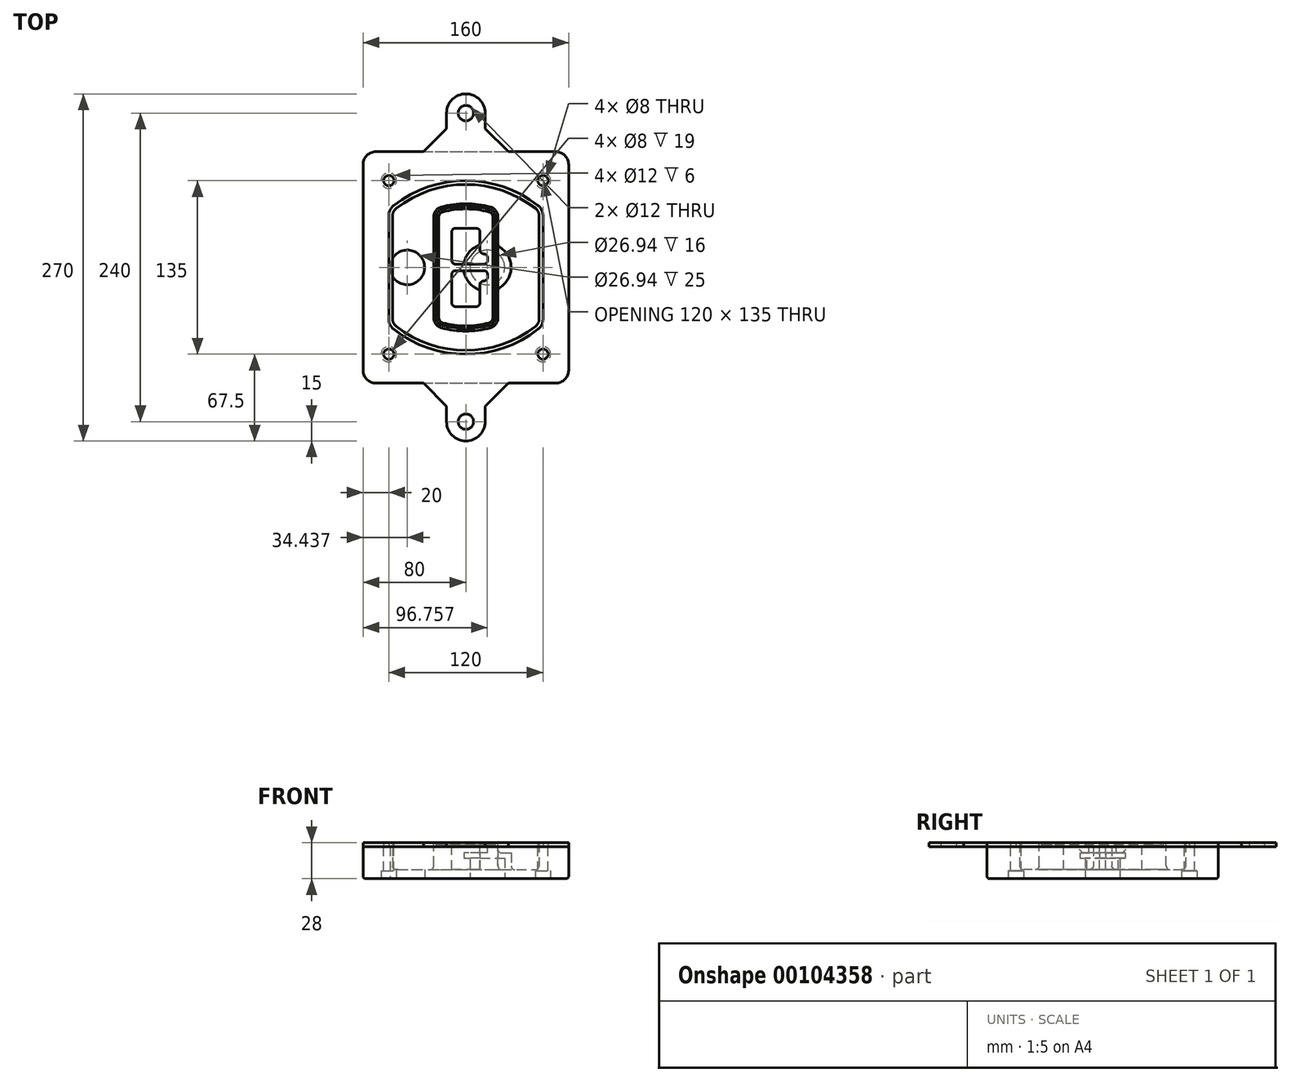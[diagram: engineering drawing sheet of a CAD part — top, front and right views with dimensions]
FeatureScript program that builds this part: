
annotation { "Feature Type Name" : "Feature", "Feature Type Description" : "" }
export const myFeature = defineFeature(function(context is Context, id is Id, definition is map)
    precondition{}
    {
        {
            var Q0;
            Q0=qCreatedBy(makeId("Top.planeOp"),FACE);
            var sketch = newSketch(context, id + "F0", { "sketchPlane" : qUnion([Q0])});
            skPoint(sketch, "E0.rect.middle", {"position": v(0, 0) * mm});
            skLineSegment(sketch, "E1.bottom", {"start": v(-70, -90) * mm, "end": v(70, -90) * mm});
            skLineSegment(sketch, "E1.top", {"start": v(-70, 90) * mm, "end": v(70, 90) * mm});
            skLineSegment(sketch, "E1.left", {"start": v(-80, -80) * mm, "end": v(-80, 80) * mm});
            skLineSegment(sketch, "E1.right", {"start": v(80, -80) * mm, "end": v(80, 80) * mm});
            skLineSegment(sketch, "E2", {"start": v(-80, 90) * mm, "end": v(80, -90) * mm, "construction": true});
            skLineSegment(sketch, "E3", {"start": v(80, 90) * mm, "end": v(-80, -90) * mm, "construction": true});
            skCircle(sketch, "E4", {"center": v(-60, 67.5) * mm, "radius": 4 * mm});
            skCircle(sketch, "E5", {"center": v(60, 67.5) * mm, "radius": 4 * mm});
            skCircle(sketch, "E6", {"center": v(60, -67.5) * mm, "radius": 4 * mm});
            skCircle(sketch, "E7", {"center": v(-60, -67.5) * mm, "radius": 4 * mm});
            skLineSegment(sketch, "E8", {"start": v(-60, 67.5) * mm, "end": v(60, 67.5) * mm, "construction": true});
            skLineSegment(sketch, "E9", {"start": v(60, 67.5) * mm, "end": v(60, -67.5) * mm, "construction": true});
            skLineSegment(sketch, "E10", {"start": v(60, -67.5) * mm, "end": v(-60, -67.5) * mm, "construction": true});
            skLineSegment(sketch, "E11", {"start": v(-60, -67.5) * mm, "end": v(-60, 67.5) * mm, "construction": true});
            skLineSegment(sketch, "E12", {"start": v(-60, 40.3) * mm, "end": v(-60, -40.3) * mm});
            skLineSegment(sketch, "E13", {"start": v(60, 40.3) * mm, "end": v(60, -40.3) * mm});
            skArc(sketch, "E14", {"start": v(56.15, 48.18) * mm, "mid": v(0, 67.5) * mm, "end": v(-56.15, 48.18) * mm});
            skArc(sketch, "E15", {"start": v(-56.15, -48.18) * mm, "mid": v(0, -67.5) * mm, "end": v(56.15, -48.18) * mm});
            skLineSegment(sketch, "E16", {"start": v(-60, 0) * mm, "end": v(60, 0) * mm, "construction": true});
            skPoint(sketch, "E17.visualSharp", {"position": v(-60, -45) * mm});
            skArc(sketch, "E17.filletArc", {"start": v(-60, -40.3) * mm, "mid": v(-58.99, -44.68) * mm, "end": v(-56.15, -48.18) * mm});
            skPoint(sketch, "E18.visualSharp", {"position": v(-60, 45) * mm});
            skArc(sketch, "E18.filletArc", {"start": v(-56.15, 48.18) * mm, "mid": v(-58.99, 44.68) * mm, "end": v(-60, 40.3) * mm});
            skPoint(sketch, "E19.visualSharp", {"position": v(60, 45) * mm});
            skArc(sketch, "E19.filletArc", {"start": v(60, 40.3) * mm, "mid": v(58.99, 44.68) * mm, "end": v(56.15, 48.18) * mm});
            skPoint(sketch, "E20.visualSharp", {"position": v(60, -45) * mm});
            skArc(sketch, "E20.filletArc", {"start": v(56.15, -48.18) * mm, "mid": v(58.99, -44.68) * mm, "end": v(60, -40.3) * mm});
            skPoint(sketch, "E21.visualSharp", {"position": v(-80, 90) * mm});
            skArc(sketch, "E21.filletArc", {"start": v(-70, 90) * mm, "mid": v(-77.07, 87.07) * mm, "end": v(-80, 80) * mm});
            skPoint(sketch, "E22.visualSharp", {"position": v(80, 90) * mm});
            skArc(sketch, "E22.filletArc", {"start": v(80, 80) * mm, "mid": v(77.07, 87.07) * mm, "end": v(70, 90) * mm});
            skPoint(sketch, "E23.visualSharp", {"position": v(80, -90) * mm});
            skArc(sketch, "E23.filletArc", {"start": v(70, -90) * mm, "mid": v(77.07, -87.07) * mm, "end": v(80, -80) * mm});
            skPoint(sketch, "E24.visualSharp", {"position": v(-80, -90) * mm});
            skArc(sketch, "E24.filletArc", {"start": v(-80, -80) * mm, "mid": v(-77.07, -87.07) * mm, "end": v(-70, -90) * mm});
            skArc(sketch, "E25.0", {"start": v(57, 40.3) * mm, "mid": v(56.3, 43.36) * mm, "end": v(54.3, 45.81) * mm});
            skLineSegment(sketch, "E25.1", {"start": v(57, 40.3) * mm, "end": v(57, -40.3) * mm});
            skArc(sketch, "E25.2", {"start": v(54.3, -45.81) * mm, "mid": v(56.3, -43.36) * mm, "end": v(57, -40.3) * mm});
            skArc(sketch, "E25.3", {"start": v(-54.3, -45.81) * mm, "mid": v(0, -64.5) * mm, "end": v(54.3, -45.81) * mm});
            skArc(sketch, "E25.4", {"start": v(-57, -40.3) * mm, "mid": v(-56.3, -43.36) * mm, "end": v(-54.3, -45.81) * mm});
            skArc(sketch, "E25.5", {"start": v(54.3, 45.81) * mm, "mid": v(0, 64.5) * mm, "end": v(-54.3, 45.81) * mm});
            skLineSegment(sketch, "E25.6", {"start": v(-57, 40.3) * mm, "end": v(-57, -40.3) * mm});
            skArc(sketch, "E25.7", {"start": v(-54.3, 45.81) * mm, "mid": v(-56.3, 43.36) * mm, "end": v(-57, 40.3) * mm});
            skArc(sketch, "E26.0", {"start": v(-58.62, 51.33) * mm, "mid": v(-62.58, 46.43) * mm, "end": v(-64, 40.3) * mm});
            skArc(sketch, "E26.1", {"start": v(58.62, 51.33) * mm, "mid": v(0, 71.5) * mm, "end": v(-58.62, 51.33) * mm});
            skArc(sketch, "E26.2", {"start": v(64, 40.3) * mm, "mid": v(62.58, 46.43) * mm, "end": v(58.62, 51.33) * mm});
            skLineSegment(sketch, "E26.3", {"start": v(64, 40.3) * mm, "end": v(64, -40.3) * mm});
            skArc(sketch, "E26.4", {"start": v(58.62, -51.33) * mm, "mid": v(62.58, -46.43) * mm, "end": v(64, -40.3) * mm});
            skLineSegment(sketch, "E26.5", {"start": v(-64, 40.3) * mm, "end": v(-64, -40.3) * mm});
            skArc(sketch, "E26.6", {"start": v(-58.62, -51.33) * mm, "mid": v(0, -71.5) * mm, "end": v(58.62, -51.33) * mm});
            skArc(sketch, "E26.7", {"start": v(-64, -40.3) * mm, "mid": v(-62.58, -46.43) * mm, "end": v(-58.62, -51.33) * mm});
            skSolve(sketch);
        }
        {
            var Q0;
            Q0=makeQuery(id+"F0.imprint","IMPRINT",FACE,{"disambiguationData":[TD([[makeQuery(id+"F0.imprint","IMPRINT",EDGE,{"derivedFrom":sQuery(id+"F0.wireOp",EDGE,"E1.bottom")}),1.0]])]});
            var Q1;
            Q1=makeQuery(id+"F0.imprint","IMPRINT",FACE,{"disambiguationData":[TD([[makeQuery(id+"F0.imprint","IMPRINT",EDGE,{"derivedFrom":sQuery(id+"F0.wireOp",EDGE,"E12")}),1.0]])]});
            var Q2;
            Q2=makeQuery(id+"F0.imprint","IMPRINT",FACE,{"disambiguationData":[TD([[makeQuery(id+"F0.imprint","IMPRINT",EDGE,{"derivedFrom":sQuery(id+"F0.wireOp",EDGE,"E25.0")}),1.0]])]});
            var Q3;
            Q3=makeQuery(id+"F0.imprint","IMPRINT",FACE,{"disambiguationData":[TD([[makeQuery(id+"F0.imprint","IMPRINT",EDGE,{"derivedFrom":sQuery(id+"F0.wireOp",EDGE,"E12")}),-1.0]])]});
            extrude(context, id + "F1", {"entities" : qUnion([Q0, Q1, Q2, Q3]), "oppositeDirection" : true, "depth" : 25 * mm});
        }
        {
            var Q0;
            Q0=makeQuery(id+"F0.imprint","IMPRINT",FACE,{"disambiguationData":[TD([[makeQuery(id+"F0.imprint","IMPRINT",EDGE,{"derivedFrom":sQuery(id+"F0.wireOp",EDGE,"E12")}),1.0]])]});
            extrude(context, id + "F2", {"entities" : qUnion([Q0]), "operationType" : NewBodyOperationType.ADD, "depth" : 3 * mm});
        }
        {
            var Q0;
            Q0=makeQuery(id+"F0.imprint","IMPRINT",FACE,{"disambiguationData":[TD([[makeQuery(id+"F0.imprint","IMPRINT",EDGE,{"derivedFrom":sQuery(id+"F0.wireOp",EDGE,"E25.0")}),1.0]])]});
            extrude(context, id + "F3", {"entities" : qUnion([Q0]), "operationType" : NewBodyOperationType.REMOVE, "oppositeDirection" : true, "depth" : 18 * mm});
        }
        {
            var Q0;
            Q0=makeQuery(id+"F2.opExtrude","CAP_FACE",FACE,{"disambiguationData":[OSD([sQuery(id+"F0.wireOp",EDGE,"E12"),sQuery(id+"F0.wireOp",EDGE,"E13"),sQuery(id+"F0.wireOp",EDGE,"E14"),sQuery(id+"F0.wireOp",EDGE,"E15"),sQuery(id+"F0.wireOp",EDGE,"E17.filletArc"),sQuery(id+"F0.wireOp",EDGE,"E18.filletArc"),sQuery(id+"F0.wireOp",EDGE,"E19.filletArc"),sQuery(id+"F0.wireOp",EDGE,"E20.filletArc"),sQuery(id+"F0.wireOp",EDGE,"E25.0"),sQuery(id+"F0.wireOp",EDGE,"E25.1"),sQuery(id+"F0.wireOp",EDGE,"E25.2"),sQuery(id+"F0.wireOp",EDGE,"E25.3"),sQuery(id+"F0.wireOp",EDGE,"E25.4"),sQuery(id+"F0.wireOp",EDGE,"E25.5"),sQuery(id+"F0.wireOp",EDGE,"E25.6"),sQuery(id+"F0.wireOp",EDGE,"E25.7")])],"isStart":false});
            var sketch = newSketch(context, id + "F4", { "sketchPlane" : qUnion([Q0])});
            skArc(sketch, "E27.0", {"start": v(-19.08, -46.97) * mm, "mid": v(0, -49.5) * mm, "end": v(19.08, -46.97) * mm});
            skArc(sketch, "E28.0", {"start": v(19.08, 46.97) * mm, "mid": v(0, 49.5) * mm, "end": v(-19.08, 46.97) * mm});
            skLineSegment(sketch, "E29", {"start": v(-25, 39.25) * mm, "end": v(-25, -39.25) * mm});
            skLineSegment(sketch, "E30", {"start": v(25, 39.25) * mm, "end": v(25, -39.25) * mm});
            skLineSegment(sketch, "E31", {"start": v(-25, 45.1) * mm, "end": v(25, 45.1) * mm, "construction": true});
            skLineSegment(sketch, "E32", {"start": v(-25, -45.1) * mm, "end": v(25, -45.1) * mm, "construction": true});
            skPoint(sketch, "E33.visualSharp", {"position": v(-25, 45.1) * mm});
            skArc(sketch, "E33.filletArc", {"start": v(-19.08, 46.97) * mm, "mid": v(-23.35, 44.11) * mm, "end": v(-25, 39.25) * mm});
            skPoint(sketch, "E34.visualSharp", {"position": v(25, 45.1) * mm});
            skArc(sketch, "E34.filletArc", {"start": v(25, 39.25) * mm, "mid": v(23.35, 44.11) * mm, "end": v(19.08, 46.97) * mm});
            skPoint(sketch, "E35.visualSharp", {"position": v(25, -45.1) * mm});
            skArc(sketch, "E35.filletArc", {"start": v(19.08, -46.97) * mm, "mid": v(23.35, -44.11) * mm, "end": v(25, -39.25) * mm});
            skPoint(sketch, "E36.visualSharp", {"position": v(-25, -45.1) * mm});
            skArc(sketch, "E36.filletArc", {"start": v(-25, -39.25) * mm, "mid": v(-23.35, -44.11) * mm, "end": v(-19.08, -46.97) * mm});
            skArc(sketch, "E37.0", {"start": v(54.3, 45.81) * mm, "mid": v(0, 64.5) * mm, "end": v(-54.3, 45.81) * mm});
            skArc(sketch, "E37.1", {"start": v(-54.3, 45.81) * mm, "mid": v(-56.3, 43.36) * mm, "end": v(-57, 40.3) * mm});
            skLineSegment(sketch, "E37.2", {"start": v(-57, 40.3) * mm, "end": v(-57, -40.3) * mm});
            skArc(sketch, "E37.3", {"start": v(-57, -40.3) * mm, "mid": v(-56.3, -43.36) * mm, "end": v(-54.3, -45.81) * mm});
            skArc(sketch, "E37.4", {"start": v(-54.3, -45.81) * mm, "mid": v(0, -64.5) * mm, "end": v(54.3, -45.81) * mm});
            skArc(sketch, "E37.5", {"start": v(54.3, -45.81) * mm, "mid": v(56.3, -43.36) * mm, "end": v(57, -40.3) * mm});
            skLineSegment(sketch, "E37.6", {"start": v(57, 40.3) * mm, "end": v(57, -40.3) * mm});
            skArc(sketch, "E37.7", {"start": v(57, 40.3) * mm, "mid": v(56.3, 43.36) * mm, "end": v(54.3, 45.81) * mm});
            skLineSegment(sketch, "E38.0", {"start": v(23, 39.25) * mm, "end": v(23, -39.25) * mm});
            skArc(sketch, "E38.1", {"start": v(18.56, -45.04) * mm, "mid": v(21.76, -42.9) * mm, "end": v(23, -39.25) * mm});
            skArc(sketch, "E38.2", {"start": v(-18.56, -45.04) * mm, "mid": v(0, -47.5) * mm, "end": v(18.56, -45.04) * mm});
            skArc(sketch, "E38.3", {"start": v(-23, -39.25) * mm, "mid": v(-21.76, -42.9) * mm, "end": v(-18.56, -45.04) * mm});
            skLineSegment(sketch, "E38.4", {"start": v(-23, 39.25) * mm, "end": v(-23, -39.25) * mm});
            skArc(sketch, "E38.5", {"start": v(23, 39.25) * mm, "mid": v(21.76, 42.9) * mm, "end": v(18.56, 45.04) * mm});
            skArc(sketch, "E38.6", {"start": v(-18.56, 45.04) * mm, "mid": v(-21.76, 42.9) * mm, "end": v(-23, 39.25) * mm});
            skArc(sketch, "E38.7", {"start": v(18.56, 45.04) * mm, "mid": v(0, 47.5) * mm, "end": v(-18.56, 45.04) * mm});
            skArc(sketch, "E39.0", {"start": v(21, 39.25) * mm, "mid": v(20.18, 41.68) * mm, "end": v(18.04, 43.1) * mm});
            skLineSegment(sketch, "E39.1", {"start": v(21, 39.25) * mm, "end": v(21, -39.25) * mm});
            skArc(sketch, "E39.2", {"start": v(18.04, -43.1) * mm, "mid": v(20.18, -41.68) * mm, "end": v(21, -39.25) * mm});
            skArc(sketch, "E39.3", {"start": v(-18.04, -43.1) * mm, "mid": v(0, -45.5) * mm, "end": v(18.04, -43.1) * mm});
            skArc(sketch, "E39.4", {"start": v(-21, -39.25) * mm, "mid": v(-20.18, -41.68) * mm, "end": v(-18.04, -43.1) * mm});
            skArc(sketch, "E39.5", {"start": v(18.04, 43.1) * mm, "mid": v(0, 45.5) * mm, "end": v(-18.04, 43.1) * mm});
            skLineSegment(sketch, "E39.6", {"start": v(-21, 39.25) * mm, "end": v(-21, -39.25) * mm});
            skArc(sketch, "E39.7", {"start": v(-18.04, 43.1) * mm, "mid": v(-20.18, 41.68) * mm, "end": v(-21, 39.25) * mm});
            skLineSegment(sketch, "E40", {"start": v(-25, 0) * mm, "end": v(25, 0) * mm, "construction": true});
            skLineSegment(sketch, "E41", {"start": v(-11, 5.5) * mm, "end": v(-11, 27.5) * mm});
            skLineSegment(sketch, "E42", {"start": v(-8, 30.5) * mm, "end": v(8, 30.5) * mm});
            skLineSegment(sketch, "E43", {"start": v(11, 27.5) * mm, "end": v(11, 13.5) * mm});
            skLineSegment(sketch, "E44", {"start": v(14, 10.5) * mm, "end": v(14, 10.5) * mm});
            skLineSegment(sketch, "E45", {"start": v(17, 7.5) * mm, "end": v(17, 5.5) * mm});
            skLineSegment(sketch, "E46", {"start": v(14, 2.5) * mm, "end": v(-8, 2.5) * mm});
            skPoint(sketch, "E47.visualSharp", {"position": v(-11, 30.5) * mm});
            skArc(sketch, "E47.filletArc", {"start": v(-8, 30.5) * mm, "mid": v(-10.12, 29.62) * mm, "end": v(-11, 27.5) * mm});
            skPoint(sketch, "E48.visualSharp", {"position": v(11, 30.5) * mm});
            skArc(sketch, "E48.filletArc", {"start": v(11, 27.5) * mm, "mid": v(10.12, 29.62) * mm, "end": v(8, 30.5) * mm});
            skPoint(sketch, "E49.visualSharp", {"position": v(11, 10.5) * mm});
            skArc(sketch, "E49.filletArc", {"start": v(11, 13.5) * mm, "mid": v(11.88, 11.38) * mm, "end": v(14, 10.5) * mm});
            skPoint(sketch, "E50.visualSharp", {"position": v(17, 10.5) * mm});
            skArc(sketch, "E50.filletArc", {"start": v(17, 7.5) * mm, "mid": v(16.12, 9.62) * mm, "end": v(14, 10.5) * mm});
            skPoint(sketch, "E51.visualSharp", {"position": v(17, 2.5) * mm});
            skArc(sketch, "E51.filletArc", {"start": v(14, 2.5) * mm, "mid": v(16.12, 3.38) * mm, "end": v(17, 5.5) * mm});
            skPoint(sketch, "E52.visualSharp", {"position": v(-11, 2.5) * mm});
            skArc(sketch, "E52.filletArc", {"start": v(-11, 5.5) * mm, "mid": v(-10.12, 3.38) * mm, "end": v(-8, 2.5) * mm});
            skLineSegment(sketch, "E53.0.MirrorCS", {"start": v(14, -2.5) * mm, "end": v(-8, -2.5) * mm});
            skArc(sketch, "E54.0.MirrorCS", {"start": v(-11, -5.5) * mm, "mid": v(-10.12, -3.38) * mm, "end": v(-8, -2.5) * mm});
            skLineSegment(sketch, "E55.0.MirrorCS", {"start": v(-11, -5.5) * mm, "end": v(-11, -27.5) * mm});
            skArc(sketch, "E56.0.MirrorCS", {"start": v(-8, -30.5) * mm, "mid": v(-10.12, -29.62) * mm, "end": v(-11, -27.5) * mm});
            skLineSegment(sketch, "E57.0.MirrorCS", {"start": v(-8, -30.5) * mm, "end": v(8, -30.5) * mm});
            skArc(sketch, "E58.0.MirrorCS", {"start": v(11, -27.5) * mm, "mid": v(10.12, -29.62) * mm, "end": v(8, -30.5) * mm});
            skLineSegment(sketch, "E59.0.MirrorCS", {"start": v(11, -27.5) * mm, "end": v(11, -13.5) * mm});
            skArc(sketch, "E60.0.MirrorCS", {"start": v(11, -13.5) * mm, "mid": v(11.88, -11.38) * mm, "end": v(14, -10.5) * mm});
            skArc(sketch, "E61.0.MirrorCS", {"start": v(17, -7.5) * mm, "mid": v(16.12, -9.62) * mm, "end": v(14, -10.5) * mm});
            skLineSegment(sketch, "E62.0.MirrorCS", {"start": v(17, -7.5) * mm, "end": v(17, -5.5) * mm});
            skArc(sketch, "E63.0.MirrorCS", {"start": v(14, -2.5) * mm, "mid": v(16.12, -3.38) * mm, "end": v(17, -5.5) * mm});
            skSolve(sketch);
        }
        {
            var Q0;
            Q0=makeQuery(id+"F4.imprint","IMPRINT",FACE,{"disambiguationData":[TD([[makeQuery(id+"F4.imprint","IMPRINT",EDGE,{"derivedFrom":sQuery(id+"F4.wireOp",EDGE,"E27.0")}),1.0]])]});
            var Q1;
            Q1=makeQuery(id+"F4.imprint","IMPRINT",FACE,{"disambiguationData":[TD([[makeQuery(id+"F4.imprint","IMPRINT",EDGE,{"derivedFrom":sQuery(id+"F4.wireOp",EDGE,"E38.0")}),-1.0]])]});
            var Q2;
            Q2=makeQuery(id+"F4.imprint","IMPRINT",FACE,{"disambiguationData":[TD([[makeQuery(id+"F4.imprint","IMPRINT",EDGE,{"derivedFrom":sQuery(id+"F4.wireOp",EDGE,"E39.0")}),1.0]])]});
            extrude(context, id + "F5", {"entities" : qUnion([Q0, Q1, Q2]), "operationType" : NewBodyOperationType.ADD, "endBound" : BoundingType.UP_TO_NEXT, "oppositeDirection" : true, "depth" : 25 * mm});
        }
        {
            var Q0;
            Q0=makeQuery(id+"F4.imprint","IMPRINT",FACE,{"disambiguationData":[TD([[makeQuery(id+"F4.imprint","IMPRINT",EDGE,{"derivedFrom":sQuery(id+"F4.wireOp",EDGE,"E38.0")}),-1.0]])]});
            extrude(context, id + "F6", {"entities" : qUnion([Q0]), "operationType" : NewBodyOperationType.REMOVE, "oppositeDirection" : true, "depth" : 2 * mm});
        }
        {
            var Q0;
            Q0=makeQuery(id+"F1.opExtrude","CAP_FACE",FACE,{"disambiguationData":[OSD([sQuery(id+"F0.wireOp",EDGE,"E1.bottom"),sQuery(id+"F0.wireOp",EDGE,"E1.top"),sQuery(id+"F0.wireOp",EDGE,"E1.left"),sQuery(id+"F0.wireOp",EDGE,"E1.right"),sQuery(id+"F0.wireOp",EDGE,"E4"),sQuery(id+"F0.wireOp",EDGE,"E5"),sQuery(id+"F0.wireOp",EDGE,"E6"),sQuery(id+"F0.wireOp",EDGE,"E7"),sQuery(id+"F0.wireOp",EDGE,"E21.filletArc"),sQuery(id+"F0.wireOp",EDGE,"E22.filletArc"),sQuery(id+"F0.wireOp",EDGE,"E23.filletArc"),sQuery(id+"F0.wireOp",EDGE,"E24.filletArc")])],"isStart":false});
            var sketch = newSketch(context, id + "F7", { "sketchPlane" : qUnion([Q0])});
            skCircle(sketch, "E64", {"center": v(16.76, 0) * mm, "radius": 13.47 * mm});
            skCircle(sketch, "E65", {"center": v(-45.56, 0) * mm, "radius": 13.47 * mm});
            skLineSegment(sketch, "E66", {"start": v(80, 0) * mm, "end": v(-80, 0) * mm});
            skCircle(sketch, "E67", {"center": v(16.76, 0) * mm, "radius": 18.47 * mm});
            skCircle(sketch, "E68", {"center": v(60, -67.5) * mm, "radius": 6 * mm});
            skCircle(sketch, "E69", {"center": v(-60, -67.5) * mm, "radius": 6 * mm});
            skCircle(sketch, "E70", {"center": v(-60, 67.5) * mm, "radius": 6 * mm});
            skCircle(sketch, "E71", {"center": v(60, 67.5) * mm, "radius": 6 * mm});
            skSolve(sketch);
        }
        {
            var Q0;
            {var subQ1=sQuery(id+"F7.wireOp",EDGE,"E66");var subQ4=sQuery(id+"F7.wireOp",EDGE,"E64");var subQ6=makeQuery(id+"F7.imprint","INTERSECT",VERTEX,{"disambiguationData":[OD(0.0)],"derivedFrom":[subQ4,subQ1]});Q0=makeQuery(id+"F7.imprint","IMPRINT",FACE,{"disambiguationData":[TD([[makeQuery(id+"F7.imprint","IMPRINT",EDGE,{"disambiguationData":[TD([[subQ6,-1.0]])],"derivedFrom":subQ4}),-1.0]])]});}
            var Q1;
            {var subQ0=sQuery(id+"F7.wireOp",EDGE,"E66");var subQ1=sQuery(id+"F7.wireOp",EDGE,"E64");var subQ3=makeQuery(id+"F7.imprint","INTERSECT",VERTEX,{"disambiguationData":[OD(0.0)],"derivedFrom":[subQ1,subQ0]});Q1=makeQuery(id+"F7.imprint","IMPRINT",FACE,{"disambiguationData":[TD([[makeQuery(id+"F7.imprint","IMPRINT",EDGE,{"disambiguationData":[TD([[subQ3,-1.0]])],"derivedFrom":subQ1}),1.0]])]});}
            var Q2;
            {var subQ0=sQuery(id+"F7.wireOp",EDGE,"E66");var subQ1=sQuery(id+"F7.wireOp",EDGE,"E64");var subQ3=makeQuery(id+"F7.imprint","INTERSECT",VERTEX,{"disambiguationData":[OD(0.0)],"derivedFrom":[subQ1,subQ0]});Q2=makeQuery(id+"F7.imprint","IMPRINT",FACE,{"disambiguationData":[TD([[makeQuery(id+"F7.imprint","IMPRINT",EDGE,{"disambiguationData":[TD([[subQ3,1.0]])],"derivedFrom":subQ1}),1.0]])]});}
            var Q3;
            {var subQ1=sQuery(id+"F7.wireOp",EDGE,"E66");var subQ4=sQuery(id+"F7.wireOp",EDGE,"E64");var subQ6=makeQuery(id+"F7.imprint","INTERSECT",VERTEX,{"disambiguationData":[OD(0.0)],"derivedFrom":[subQ4,subQ1]});Q3=makeQuery(id+"F7.imprint","IMPRINT",FACE,{"disambiguationData":[TD([[makeQuery(id+"F7.imprint","IMPRINT",EDGE,{"disambiguationData":[TD([[subQ6,1.0]])],"derivedFrom":subQ4}),-1.0]])]});}
            extrude(context, id + "F8", {"entities" : qUnion([Q0, Q1, Q2, Q3]), "operationType" : NewBodyOperationType.ADD, "oppositeDirection" : true, "depth" : 20 * mm});
        }
        {
            var Q0;
            {var subQ0=sQuery(id+"F7.wireOp",EDGE,"E66");var subQ1=sQuery(id+"F7.wireOp",EDGE,"E64");var subQ3=makeQuery(id+"F7.imprint","INTERSECT",VERTEX,{"disambiguationData":[OD(0.0)],"derivedFrom":[subQ1,subQ0]});Q0=makeQuery(id+"F7.imprint","IMPRINT",FACE,{"disambiguationData":[TD([[makeQuery(id+"F7.imprint","IMPRINT",EDGE,{"disambiguationData":[TD([[subQ3,-1.0]])],"derivedFrom":subQ1}),1.0]])]});}
            var Q1;
            {var subQ0=sQuery(id+"F7.wireOp",EDGE,"E66");var subQ1=sQuery(id+"F7.wireOp",EDGE,"E64");var subQ3=makeQuery(id+"F7.imprint","INTERSECT",VERTEX,{"disambiguationData":[OD(0.0)],"derivedFrom":[subQ1,subQ0]});Q1=makeQuery(id+"F7.imprint","IMPRINT",FACE,{"disambiguationData":[TD([[makeQuery(id+"F7.imprint","IMPRINT",EDGE,{"disambiguationData":[TD([[subQ3,1.0]])],"derivedFrom":subQ1}),1.0]])]});}
            extrude(context, id + "F9", {"entities" : qUnion([Q0, Q1]), "operationType" : NewBodyOperationType.REMOVE, "oppositeDirection" : true, "depth" : 16 * mm});
        }
        {
            var Q0;
            {var subQ0=sQuery(id+"F7.wireOp",EDGE,"E66");var subQ1=sQuery(id+"F7.wireOp",EDGE,"E65");var subQ3=makeQuery(id+"F7.imprint","INTERSECT",VERTEX,{"disambiguationData":[OD(0.0)],"derivedFrom":[subQ1,subQ0]});Q0=makeQuery(id+"F7.imprint","IMPRINT",FACE,{"disambiguationData":[TD([[makeQuery(id+"F7.imprint","IMPRINT",EDGE,{"disambiguationData":[TD([[subQ3,-1.0]])],"derivedFrom":subQ1}),1.0]])]});}
            var Q1;
            {var subQ0=sQuery(id+"F7.wireOp",EDGE,"E66");var subQ1=sQuery(id+"F7.wireOp",EDGE,"E65");var subQ3=makeQuery(id+"F7.imprint","INTERSECT",VERTEX,{"disambiguationData":[OD(0.0)],"derivedFrom":[subQ1,subQ0]});Q1=makeQuery(id+"F7.imprint","IMPRINT",FACE,{"disambiguationData":[TD([[makeQuery(id+"F7.imprint","IMPRINT",EDGE,{"disambiguationData":[TD([[subQ3,1.0]])],"derivedFrom":subQ1}),1.0]])]});}
            extrude(context, id + "F10", {"entities" : qUnion([Q0, Q1]), "operationType" : NewBodyOperationType.REMOVE, "oppositeDirection" : true, "depth" : 25 * mm});
        }
        {
            var Q0;
            Q0=makeQuery(id+"F7.imprint","IMPRINT",FACE,{"disambiguationData":[TD([[makeQuery(id+"F7.imprint","IMPRINT",EDGE,{"derivedFrom":sQuery(id+"F7.wireOp",EDGE,"E68")}),1.0]])]});
            var Q1;
            Q1=makeQuery(id+"F7.imprint","IMPRINT",FACE,{"disambiguationData":[TD([[makeQuery(id+"F7.imprint","IMPRINT",EDGE,{"derivedFrom":makeQuery(id+"F1.opExtrude","CAP_EDGE",EDGE,{"disambiguationData":[OSD([sQuery(id+"F0.wireOp",EDGE,"E5")])],"isStart":false})}),-1.0]])]});
            var Q2;
            Q2=makeQuery(id+"F7.imprint","IMPRINT",FACE,{"disambiguationData":[TD([[makeQuery(id+"F7.imprint","IMPRINT",EDGE,{"derivedFrom":sQuery(id+"F7.wireOp",EDGE,"E69")}),1.0]])]});
            var Q3;
            Q3=makeQuery(id+"F7.imprint","IMPRINT",FACE,{"disambiguationData":[TD([[makeQuery(id+"F7.imprint","IMPRINT",EDGE,{"derivedFrom":makeQuery(id+"F1.opExtrude","CAP_EDGE",EDGE,{"disambiguationData":[OSD([sQuery(id+"F0.wireOp",EDGE,"E4")])],"isStart":false})}),-1.0]])]});
            var Q4;
            Q4=makeQuery(id+"F7.imprint","IMPRINT",FACE,{"disambiguationData":[TD([[makeQuery(id+"F7.imprint","IMPRINT",EDGE,{"derivedFrom":sQuery(id+"F7.wireOp",EDGE,"E70")}),1.0]])]});
            var Q5;
            Q5=makeQuery(id+"F7.imprint","IMPRINT",FACE,{"disambiguationData":[TD([[makeQuery(id+"F7.imprint","IMPRINT",EDGE,{"derivedFrom":makeQuery(id+"F1.opExtrude","CAP_EDGE",EDGE,{"disambiguationData":[OSD([sQuery(id+"F0.wireOp",EDGE,"E7")])],"isStart":false})}),-1.0]])]});
            var Q6;
            Q6=makeQuery(id+"F7.imprint","IMPRINT",FACE,{"disambiguationData":[TD([[makeQuery(id+"F7.imprint","IMPRINT",EDGE,{"derivedFrom":sQuery(id+"F7.wireOp",EDGE,"E71")}),1.0]])]});
            var Q7;
            Q7=makeQuery(id+"F7.imprint","IMPRINT",FACE,{"disambiguationData":[TD([[makeQuery(id+"F7.imprint","IMPRINT",EDGE,{"derivedFrom":makeQuery(id+"F1.opExtrude","CAP_EDGE",EDGE,{"disambiguationData":[OSD([sQuery(id+"F0.wireOp",EDGE,"E6")])],"isStart":false})}),-1.0]])]});
            extrude(context, id + "F11", {"entities" : qUnion([Q0, Q1, Q2, Q3, Q4, Q5, Q6, Q7]), "operationType" : NewBodyOperationType.REMOVE, "oppositeDirection" : true, "depth" : 6 * mm});
        }
        {
            var Q0;
            Q0=makeQuery(id+"F9.boolean.opBoolean","COPY",FACE,{"derivedFrom":makeQuery(id+"F9.opExtrude","CAP_FACE",FACE,{"disambiguationData":[OSD([sQuery(id+"F7.wireOp",EDGE,"E64")])],"isStart":false})});
            var sketch = newSketch(context, id + "F12", { "sketchPlane" : qUnion([Q0])});
            skArc(sketch, "E72.0", {"start": v(11, 17.55) * mm, "mid": v(2.57, 11.82) * mm, "end": v(-1.54, 2.5) * mm});
            skArc(sketch, "E72.1", {"start": v(-1.54, -2.5) * mm, "mid": v(2.57, -11.82) * mm, "end": v(11, -17.55) * mm});
            skLineSegment(sketch, "E73", {"start": v(-1.54, -2.5) * mm, "end": v(14, -2.5) * mm});
            skLineSegment(sketch, "E74.0", {"start": v(14, 2.5) * mm, "end": v(-1.54, 2.5) * mm});
            skArc(sketch, "E74.1", {"start": v(14, 2.5) * mm, "mid": v(16.12, 3.38) * mm, "end": v(17, 5.5) * mm});
            skLineSegment(sketch, "E74.2", {"start": v(17, 7.5) * mm, "end": v(17, 5.5) * mm});
            skArc(sketch, "E74.3", {"start": v(17, 7.5) * mm, "mid": v(16.12, 9.62) * mm, "end": v(14, 10.5) * mm});
            skArc(sketch, "E74.4", {"start": v(11, 13.5) * mm, "mid": v(11.88, 11.38) * mm, "end": v(14, 10.5) * mm});
            skLineSegment(sketch, "E74.5", {"start": v(11, 17.55) * mm, "end": v(11, 13.5) * mm});
            skLineSegment(sketch, "E74.7", {"start": v(14, -2.5) * mm, "end": v(-1.54, -2.5) * mm});
            skArc(sketch, "E74.8", {"start": v(14, -2.5) * mm, "mid": v(16.12, -3.38) * mm, "end": v(17, -5.5) * mm});
            skLineSegment(sketch, "E74.9", {"start": v(17, -7.5) * mm, "end": v(17, -5.5) * mm});
            skArc(sketch, "E74.10", {"start": v(17, -7.5) * mm, "mid": v(16.12, -9.62) * mm, "end": v(14, -10.5) * mm});
            skArc(sketch, "E74.11", {"start": v(11, -13.5) * mm, "mid": v(11.88, -11.38) * mm, "end": v(14, -10.5) * mm});
            skLineSegment(sketch, "E74.12", {"start": v(11, -17.55) * mm, "end": v(11, -13.5) * mm});
            skPoint(sketch, "E75.orphan", {"position": v(11, -27.5) * mm});
            skPoint(sketch, "E76.orphan", {"position": v(-8, -2.5) * mm});
            skPoint(sketch, "E77.orphan", {"position": v(-8, 2.5) * mm});
            skPoint(sketch, "E78.orphan", {"position": v(11, 27.5) * mm});
            skSolve(sketch);
        }
        {
            var Q0;
            {var subQ7=sQuery(id+"F12.wireOp",EDGE,"E72.0");var subQ14=sQuery(id+"F12.wireOp",EDGE,"E72.1");var subQ16=sQuery(id+"F12.wireOp",EDGE,"E74.1");var subQ18=sQuery(id+"F12.wireOp",EDGE,"E74.8");Q0=qUnion([makeQuery(id+"F12.imprint","IMPRINT",FACE,{"disambiguationData":[TD([[makeQuery(id+"F12.imprint","IMPRINT",EDGE,{"derivedFrom":subQ7}),1.0]])]}),makeQuery(id+"F12.imprint","IMPRINT",FACE,{"disambiguationData":[TD([[makeQuery(id+"F12.imprint","IMPRINT",EDGE,{"derivedFrom":subQ14}),1.0]])]}),makeQuery(id+"F12.imprint","IMPRINT",FACE,{"disambiguationData":[TD([[makeQuery(id+"F12.imprint","IMPRINT",EDGE,{"derivedFrom":subQ16}),1.0]])]}),makeQuery(id+"F12.imprint","IMPRINT",FACE,{"disambiguationData":[TD([[makeQuery(id+"F12.imprint","IMPRINT",EDGE,{"derivedFrom":subQ18}),-1.0]])]})]);}
            var Q1;
            Q1=makeQuery(id+"F5.boolean.opBoolean","SPLIT",FACE,{"disambiguationData":[TD([makeQuery(id+"F5.opExtrude","SWEPT_FACE",FACE,{"disambiguationData":[OSD([sQuery(id+"F4.wireOp",EDGE,"E41")])]})])],"derivedFrom":makeQuery(id+"F3.boolean.opBoolean","COPY",FACE,{"derivedFrom":makeQuery(id+"F3.opExtrude","CAP_FACE",FACE,{"disambiguationData":[OSD([sQuery(id+"F0.wireOp",EDGE,"E25.0"),sQuery(id+"F0.wireOp",EDGE,"E25.1"),sQuery(id+"F0.wireOp",EDGE,"E25.2"),sQuery(id+"F0.wireOp",EDGE,"E25.3"),sQuery(id+"F0.wireOp",EDGE,"E25.4"),sQuery(id+"F0.wireOp",EDGE,"E25.5"),sQuery(id+"F0.wireOp",EDGE,"E25.6"),sQuery(id+"F0.wireOp",EDGE,"E25.7")])],"isStart":false})})});
            extrude(context, id + "F13", {"entities" : qUnion([Q0]), "operationType" : NewBodyOperationType.REMOVE, "endBound" : BoundingType.UP_TO_SURFACE, "endBoundEntityFace" : qUnion([Q1]), "depth" : 25 * mm});
        }
        {
            var Q0;
            Q0=makeQuery(id+"F3.boolean.opBoolean","COPY",EDGE,{"derivedFrom":makeQuery(id+"F3.opExtrude","CAP_EDGE",EDGE,{"disambiguationData":[OSD([sQuery(id+"F0.wireOp",EDGE,"E25.6")])],"isStart":false})});
            var Q1;
            Q1=makeQuery(id+"F8.boolean.opBoolean","INTERSECT",EDGE,{"derivedFrom":[makeQuery(id+"F5.opExtrude","SWEPT_FACE",FACE,{"disambiguationData":[OSD([sQuery(id+"F4.wireOp",EDGE,"E30")])]}),makeQuery(id+"F8.opExtrude","CAP_FACE",FACE,{"disambiguationData":[OSD([sQuery(id+"F7.wireOp",EDGE,"E67")])],"isStart":false})]});
            var Q2;
            Q2=makeQuery(id+"F8.boolean.opBoolean","INTERSECT",EDGE,{"disambiguationData":[OD(1.0)],"derivedFrom":[makeQuery(id+"F5.opExtrude","SWEPT_FACE",FACE,{"disambiguationData":[OSD([sQuery(id+"F4.wireOp",EDGE,"E30")])]}),makeQuery(id+"F8.opExtrude","SWEPT_FACE",FACE,{"disambiguationData":[OSD([sQuery(id+"F7.wireOp",EDGE,"E67")])]})]});
            var Q3;
            {var subQ0=sQuery(id+"F4.wireOp",EDGE,"E30");Q3=makeQuery(id+"F8.boolean.opBoolean","SPLIT",EDGE,{"disambiguationData":[TD([makeQuery(id+"F5.opExtrude","SWEPT_FACE",FACE,{"disambiguationData":[OSD([sQuery(id+"F4.wireOp",EDGE,"E35.filletArc")])]})])],"derivedFrom":makeQuery(id+"F5.opExtrude","CAP_EDGE",EDGE,{"disambiguationData":[OSD([subQ0])],"isStart":false})});}
            var Q4;
            {var subQ0=sQuery(id+"F0.wireOp",EDGE,"E25.7");var subQ1=sQuery(id+"F0.wireOp",EDGE,"E25.1");var subQ2=sQuery(id+"F0.wireOp",EDGE,"E25.6");var subQ3=sQuery(id+"F0.wireOp",EDGE,"E25.5");var subQ4=sQuery(id+"F0.wireOp",EDGE,"E25.4");var subQ5=sQuery(id+"F0.wireOp",EDGE,"E25.0");var subQ6=sQuery(id+"F0.wireOp",EDGE,"E25.2");var subQ7=sQuery(id+"F0.wireOp",EDGE,"E25.3");Q4=makeQuery(id+"F8.boolean.opBoolean","INTERSECT",EDGE,{"derivedFrom":[makeQuery(id+"F5.boolean.opBoolean","SPLIT",FACE,{"disambiguationData":[TD([makeQuery(id+"F2.opExtrude","SWEPT_FACE",FACE,{"disambiguationData":[OSD([subQ5])]})])],"derivedFrom":makeQuery(id+"F3.boolean.opBoolean","COPY",FACE,{"derivedFrom":makeQuery(id+"F3.opExtrude","CAP_FACE",FACE,{"disambiguationData":[OSD([subQ5,subQ1,subQ6,subQ7,subQ4,subQ3,subQ2,subQ0])],"isStart":false})})}),makeQuery(id+"F8.opExtrude","SWEPT_FACE",FACE,{"disambiguationData":[OSD([sQuery(id+"F7.wireOp",EDGE,"E67")])]})]});}
            var Q5;
            Q5=makeQuery(id+"F8.boolean.opBoolean","INTERSECT",EDGE,{"disambiguationData":[OD(0.0)],"derivedFrom":[makeQuery(id+"F5.opExtrude","SWEPT_FACE",FACE,{"disambiguationData":[OSD([sQuery(id+"F4.wireOp",EDGE,"E30")])]}),makeQuery(id+"F8.opExtrude","SWEPT_FACE",FACE,{"disambiguationData":[OSD([sQuery(id+"F7.wireOp",EDGE,"E67")])]})]});
            fillet(context, id + "F14", {"entities" : qUnion([Q0, Q1, Q2, Q3, Q4, Q5]), "radius" : 3 * mm, "tangentPropagation" : true, "allowEdgeOverflow" : false});
        }
        {
            var Q0;
            Q0=makeQuery(id+"F1.opExtrude","CAP_EDGE",EDGE,{"disambiguationData":[OSD([sQuery(id+"F0.wireOp",EDGE,"E1.bottom")])],"isStart":false});
            fillet(context, id + "F15", {"entities" : qUnion([Q0]), "radius" : 2 * mm, "tangentPropagation" : true, "allowEdgeOverflow" : false});
        }
        {
            var Q0;
            {var subQ0=sQuery(id+"F0.wireOp",EDGE,"E22.filletArc");var subQ1=sQuery(id+"F0.wireOp",EDGE,"E7");var subQ2=sQuery(id+"F0.wireOp",EDGE,"E6");var subQ3=sQuery(id+"F0.wireOp",EDGE,"E5");var subQ4=sQuery(id+"F0.wireOp",EDGE,"E4");var subQ5=sQuery(id+"F0.wireOp",EDGE,"E1.bottom");var subQ6=sQuery(id+"F0.wireOp",EDGE,"E21.filletArc");var subQ7=sQuery(id+"F0.wireOp",EDGE,"E1.top");var subQ8=sQuery(id+"F0.wireOp",EDGE,"E1.left");var subQ9=sQuery(id+"F0.wireOp",EDGE,"E1.right");var subQ10=sQuery(id+"F0.wireOp",EDGE,"E23.filletArc");var subQ11=sQuery(id+"F0.wireOp",EDGE,"E24.filletArc");Q0=makeQuery(id+"F2.boolean.opBoolean","SPLIT",FACE,{"disambiguationData":[TD([makeQuery(id+"F1.opExtrude","SWEPT_FACE",FACE,{"disambiguationData":[OSD([subQ5])]})])],"derivedFrom":makeQuery(id+"F1.opExtrude","CAP_FACE",FACE,{"disambiguationData":[OSD([subQ5,subQ7,subQ8,subQ9,subQ4,subQ3,subQ2,subQ1,subQ6,subQ0,subQ10,subQ11])],"isStart":true})});}
            var sketch = newSketch(context, id + "F16", { "sketchPlane" : qUnion([Q0])});
            skLineSegment(sketch, "E79", {"start": v(0, 90) * mm, "end": v(0, 120) * mm, "construction": true});
            skCircle(sketch, "E80", {"center": v(0, 120) * mm, "radius": 6 * mm});
            skLineSegment(sketch, "E81", {"start": v(-33, 90) * mm, "end": v(-15, 108) * mm});
            skLineSegment(sketch, "E82", {"start": v(-15, 108) * mm, "end": v(-15, 120) * mm});
            skLineSegment(sketch, "E83", {"start": v(15, 108) * mm, "end": v(33, 90) * mm});
            skLineSegment(sketch, "E84", {"start": v(15, 108) * mm, "end": v(15, 120) * mm});
            skArc(sketch, "E85", {"start": v(15, 120) * mm, "mid": v(0, 135) * mm, "end": v(-15, 120) * mm});
            skLineSegment(sketch, "E86", {"start": v(-80, 0) * mm, "end": v(80, 0) * mm, "construction": true});
            skLineSegment(sketch, "E87.MirrorCS", {"start": v(-33, -90) * mm, "end": v(-15, -108) * mm});
            skLineSegment(sketch, "E88.MirrorCS", {"start": v(-15, -108) * mm, "end": v(-15, -120) * mm});
            skArc(sketch, "E89.MirrorCS", {"start": v(15, -120) * mm, "mid": v(0, -135) * mm, "end": v(-15, -120) * mm});
            skLineSegment(sketch, "E90.MirrorCS", {"start": v(15, -108) * mm, "end": v(33, -90) * mm});
            skLineSegment(sketch, "E91.MirrorCS", {"start": v(15, -108) * mm, "end": v(15, -120) * mm});
            skCircle(sketch, "E92.MirrorC", {"center": v(0, -120) * mm, "radius": 6 * mm});
            skSolve(sketch);
        }
        {
            var Q0;
            {var subQ1=sQuery(id+"F16.wireOp",EDGE,"E87.MirrorCS");Q0=makeQuery(id+"F16.imprint","IMPRINT",FACE,{"disambiguationData":[TD([[makeQuery(id+"F16.imprint","IMPRINT",EDGE,{"derivedFrom":subQ1}),1.0]])]});}
            var Q1;
            Q1=makeQuery(id+"F16.imprint","IMPRINT",FACE,{"disambiguationData":[TD([[makeQuery(id+"F16.imprint","IMPRINT",EDGE,{"derivedFrom":makeQuery(id+"F1.opExtrude","CAP_EDGE",EDGE,{"disambiguationData":[OSD([sQuery(id+"F0.wireOp",EDGE,"E1.left")])],"isStart":true})}),-1.0]])]});
            var Q2;
            Q2=makeQuery(id+"F16.imprint","IMPRINT",FACE,{"disambiguationData":[TD([[makeQuery(id+"F16.imprint","IMPRINT",EDGE,{"derivedFrom":sQuery(id+"F16.wireOp",EDGE,"E80")}),-1.0]])]});
            var Q3;
            Q3=makeQuery(id+"F2.opExtrude","CAP_FACE",FACE,{"disambiguationData":[OSD([sQuery(id+"F0.wireOp",EDGE,"E12"),sQuery(id+"F0.wireOp",EDGE,"E13"),sQuery(id+"F0.wireOp",EDGE,"E14"),sQuery(id+"F0.wireOp",EDGE,"E15"),sQuery(id+"F0.wireOp",EDGE,"E17.filletArc"),sQuery(id+"F0.wireOp",EDGE,"E18.filletArc"),sQuery(id+"F0.wireOp",EDGE,"E19.filletArc"),sQuery(id+"F0.wireOp",EDGE,"E20.filletArc"),sQuery(id+"F0.wireOp",EDGE,"E25.0"),sQuery(id+"F0.wireOp",EDGE,"E25.1"),sQuery(id+"F0.wireOp",EDGE,"E25.2"),sQuery(id+"F0.wireOp",EDGE,"E25.3"),sQuery(id+"F0.wireOp",EDGE,"E25.4"),sQuery(id+"F0.wireOp",EDGE,"E25.5"),sQuery(id+"F0.wireOp",EDGE,"E25.6"),sQuery(id+"F0.wireOp",EDGE,"E25.7")])],"isStart":false});
            extrude(context, id + "F17", {"entities" : qUnion([Q0, Q1, Q2]), "endBound" : BoundingType.UP_TO_SURFACE, "endBoundEntityFace" : qUnion([Q3]), "depth" : 25 * mm});
        }
    });
